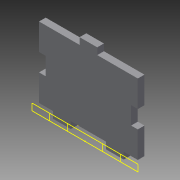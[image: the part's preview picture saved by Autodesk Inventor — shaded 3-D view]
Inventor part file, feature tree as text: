
AUTODESK INVENTOR PART (.ipt)
format: ipt  version: 2015 SP1 (Build 190203100, 203)  size: 115,712 bytes
history: native  units: in
note: dims shown in document units (in); Inventor stores cm internally (conversion verified against a paired STEP export)
features: reference x7, sketch x3, extrude x2, plane x1
ambient origin geometry x8: Origin, YZ Plane, XZ Plane, XY Plane, X Axis, Y Axis, Z Axis, Center Point
bodies: Solid1 (feature_tree)
feature tree (13):
  sketch  "Sketch1"  dims[d0=2.0in d2=0.5in]
  plane  "Work Plane1"
  extrude  "Extrusion1"  Depth=0.5in
  extrude  "Extrusion2"  Depth=0.19in TaperAngle=0.0deg
  reference  "Reference1"
  reference  "Reference2"
  reference  "Reference3"
  sketch  "Sketch2"  dims[d5=0.19in d6=0.19in d7=0.0in]
  reference  "Reference4"
  reference  "Reference5"
  reference  "Reference6"
  reference  "Reference7"
  sketch  "Sketch3"  dims[d8=0.5in d9=0.19in d10=1.15in d11=0.19in d12=0.0in d13=0.75in d14=0.75in d15=0.5in]
